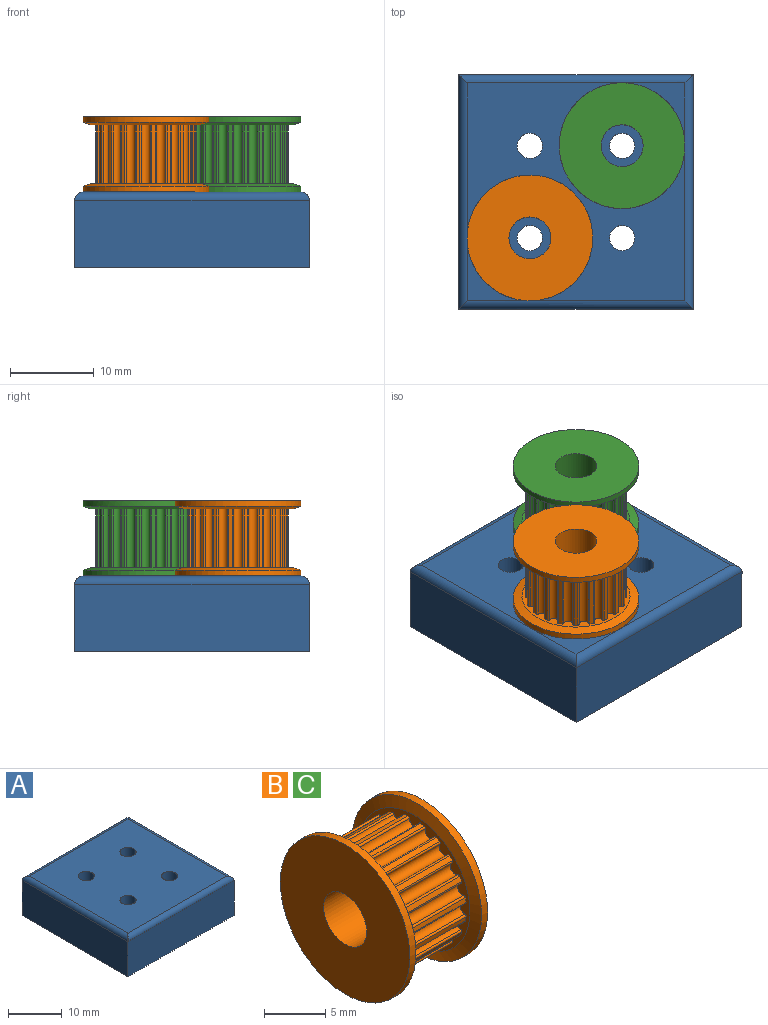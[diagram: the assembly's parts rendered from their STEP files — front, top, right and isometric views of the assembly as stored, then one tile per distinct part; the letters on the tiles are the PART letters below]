
ASSEMBLY  parts=3 mates=2
PART A: 14 faces, bbox 28x28x9 mm
  f0: plane 28x8mm, normal (0,-1,0), area 224mm2, adj f1,f3,f5,f10
  f1: plane 28x8mm, normal (1,0,0), area 224mm2, adj f0,f2,f5,f11
  f2: plane 28x8mm, normal (0,1,0), area 224mm2, adj f1,f3,f5,f13
  f3: plane 28x8mm, normal (-1,0,0), area 224mm2, adj f0,f2,f5,f12
  f4: plane 26x26mm, normal (0,0,1), area 647.7mm2, adj f6,f7,f8,f9,f10,f11,f12,f13
  f5: plane 28x28mm, normal (0,0,-1), area 755.7mm2, adj f0,f1,f2,f3,f6,f7,f8,f9
  f6: cylinder r=1.5mm len=9mm, axis (0,0,1), area 84.8mm2, adj f4,f5
  f7: cylinder r=1.5mm len=9mm, axis (0,0,1), area 84.8mm2, adj f4,f5
  f8: cylinder r=1.5mm len=9mm, axis (0,0,1), area 84.8mm2, adj f4,f5
  f9: cylinder r=1.5mm len=9mm, axis (0,0,1), area 84.8mm2, adj f4,f5
  f10: cylinder r=1mm len=28mm, axis (-1,0,0), area 42.8mm2, adj f0,f4,f11,f12
  f11: cylinder r=1mm len=28mm, axis (0,-1,0), area 42.8mm2, adj f1,f4,f10,f13
  f12: cylinder r=1mm len=28mm, axis (0,1,0), area 42.8mm2, adj f3,f4,f10,f13
  f13: cylinder r=1mm len=28mm, axis (1,0,0), area 42.8mm2, adj f2,f4,f11,f12
PART B: 93 faces, bbox 9x15x15 mm
  f0: cylinder r=7.5mm len=15mm, axis (-1,0,0), area 33.3mm2, adj f25,f92
  f1: cylinder r=2.5mm len=8.8mm, axis (1,0,0), area 138.2mm2, adj f91,f92
  f2: cylinder r=6.05mm len=7mm, axis (-1,0,0), area 3.2mm2, adj f23,f24,f83,f90
  f3: cylinder r=6.05mm len=7mm, axis (-1,0,0), area 3.2mm2, adj f23,f24,f82,f84
  f4: cylinder r=6.05mm len=7mm, axis (-1,0,0), area 3.2mm2, adj f23,f24,f81,f85
  f5: cylinder r=6.05mm len=7mm, axis (-1,0,0), area 3.2mm2, adj f23,f24,f80,f88
  f6: cylinder r=6.05mm len=7mm, axis (-1,0,0), area 3.2mm2, adj f23,f24,f79,f87
  f7: cylinder r=6.05mm len=7mm, axis (-1,0,0), area 3.2mm2, adj f23,f24,f78,f86
  f8: cylinder r=6.05mm len=7mm, axis (-1,0,0), area 3.2mm2, adj f23,f24,f76,f77
  f9: cylinder r=6.05mm len=7mm, axis (-1,0,0), area 3.2mm2, adj f23,f24,f74,f75
  f10: cylinder r=6.05mm len=7mm, axis (-1,0,0), area 3.2mm2, adj f23,f24,f72,f73
  f11: cylinder r=6.05mm len=7mm, axis (-1,0,0), area 3.2mm2, adj f23,f24,f70,f71
  f12: cylinder r=6.05mm len=7mm, axis (-1,0,0), area 3.2mm2, adj f23,f24,f68,f69
  f13: cylinder r=6.05mm len=7mm, axis (-1,0,0), area 3.2mm2, adj f23,f24,f66,f67
  f14: cylinder r=6.05mm len=7mm, axis (-1,0,0), area 3.2mm2, adj f23,f24,f64,f65
  f15: cylinder r=6.05mm len=7mm, axis (-1,0,0), area 3.2mm2, adj f23,f24,f62,f63
  f16: cylinder r=6.05mm len=7mm, axis (-1,0,0), area 3.2mm2, adj f23,f24,f60,f61
  f17: cylinder r=6.05mm len=7mm, axis (-1,0,0), area 3.2mm2, adj f23,f24,f51,f89
  f18: cylinder r=6.05mm len=7mm, axis (-1,0,0), area 3.2mm2, adj f23,f24,f58,f59
  f19: cylinder r=6.05mm len=7mm, axis (-1,0,0), area 3.2mm2, adj f23,f24,f56,f57
  f20: cylinder r=6.05mm len=7mm, axis (-1,0,0), area 3.2mm2, adj f23,f24,f54,f55
  f21: cylinder r=6.05mm len=7mm, axis (-1,0,0), area 3.2mm2, adj f23,f24,f52,f53
  f22: cone r=6.45mm half-angle=74.4deg, axis (1,0,0), area 47.8mm2, adj f23,f30
  f23: plane 12.9x12.9mm, normal (-1,0,0), area 29.5mm2, adj f2,f3,f4,f5,f6,f7,f8,f9
  f24: plane 12.9x12.9mm, normal (1,0,0), area 29.5mm2, adj f2,f3,f4,f5,f6,f7,f8,f9
  f25: cone r=7.5mm half-angle=74.4deg, axis (-1,0,0), area 47.8mm2, adj f0,f24
  f26: plane 8.34x8.34mm, normal (1,0,0), area 31.7mm2, adj f27,f91
  f27: cone r=4.25mm half-angle=45.3deg, axis (-1,0,0), area 3mm2, adj f26,f28
  f28: cone r=4.33mm half-angle=44.7deg, axis (1,0,0), area 3mm2, adj f27,f29
  f29: plane 15x15mm, normal (1,0,0), area 117.9mm2, adj f28,f30
  f30: cylinder r=7.5mm len=15mm, axis (-1,0,0), area 33.3mm2, adj f22,f29
  f31: cylinder r=0.55mm len=7mm, axis (-1,0,0), area 12.1mm2, adj f23,f24,f51,f52
  f32: cylinder r=0.55mm len=7mm, axis (-1,0,0), area 12.1mm2, adj f23,f24,f53,f54
  f33: cylinder r=0.55mm len=7mm, axis (-1,0,0), area 12.1mm2, adj f23,f24,f55,f56
  f34: cylinder r=0.55mm len=7mm, axis (-1,0,0), area 12.1mm2, adj f23,f24,f57,f58
  f35: cylinder r=0.55mm len=7mm, axis (-1,0,0), area 12.1mm2, adj f23,f24,f59,f60
  f36: cylinder r=0.55mm len=7mm, axis (-1,0,0), area 12.1mm2, adj f23,f24,f89,f90
  f37: cylinder r=0.55mm len=7mm, axis (-1,0,0), area 12.1mm2, adj f23,f24,f61,f62
  f38: cylinder r=0.55mm len=7mm, axis (-1,0,0), area 12.1mm2, adj f23,f24,f63,f64
  f39: cylinder r=0.55mm len=7mm, axis (-1,0,0), area 12.1mm2, adj f23,f24,f65,f66
  f40: cylinder r=0.55mm len=7mm, axis (-1,0,0), area 12.1mm2, adj f23,f24,f67,f68
  f41: cylinder r=0.55mm len=7mm, axis (-1,0,0), area 12.1mm2, adj f23,f24,f69,f70
  f42: cylinder r=0.55mm len=7mm, axis (-1,0,0), area 12.1mm2, adj f23,f24,f71,f72
  f43: cylinder r=0.55mm len=7mm, axis (-1,0,0), area 12.1mm2, adj f23,f24,f73,f74
  f44: cylinder r=0.55mm len=7mm, axis (-1,0,0), area 12.1mm2, adj f23,f24,f75,f76
  f45: cylinder r=0.55mm len=7mm, axis (-1,0,0), area 12.1mm2, adj f23,f24,f77,f78
  f46: cylinder r=0.55mm len=7mm, axis (-1,0,0), area 12.1mm2, adj f23,f24,f79,f86
  f47: cylinder r=0.55mm len=7mm, axis (-1,0,0), area 12.1mm2, adj f23,f24,f80,f87
  f48: cylinder r=0.55mm len=7mm, axis (-1,0,0), area 12.1mm2, adj f23,f24,f81,f88
  f49: cylinder r=0.55mm len=7mm, axis (-1,0,0), area 12.1mm2, adj f23,f24,f82,f85
  f50: cylinder r=0.55mm len=7mm, axis (-1,0,0), area 12.1mm2, adj f23,f24,f83,f84
  f51: cylinder r=0.15mm len=7mm, axis (1,0,0), area 1.8mm2, adj f17,f23,f24,f31
  f52: cylinder r=0.15mm len=7mm, axis (-1,0,0), area 1.8mm2, adj f21,f23,f24,f31
  f53: cylinder r=0.15mm len=7mm, axis (1,0,0), area 1.8mm2, adj f21,f23,f24,f32
  f54: cylinder r=0.15mm len=7mm, axis (-1,0,0), area 1.8mm2, adj f20,f23,f24,f32
  f55: cylinder r=0.15mm len=7mm, axis (1,0,0), area 1.8mm2, adj f20,f23,f24,f33
  f56: cylinder r=0.15mm len=7mm, axis (-1,0,0), area 1.8mm2, adj f19,f23,f24,f33
  f57: cylinder r=0.15mm len=7mm, axis (1,0,0), area 1.8mm2, adj f19,f23,f24,f34
  f58: cylinder r=0.15mm len=7mm, axis (-1,0,0), area 1.8mm2, adj f18,f23,f24,f34
  f59: cylinder r=0.15mm len=7mm, axis (1,0,0), area 1.8mm2, adj f18,f23,f24,f35
  f60: cylinder r=0.15mm len=7mm, axis (-1,0,0), area 1.8mm2, adj f16,f23,f24,f35
  f61: cylinder r=0.15mm len=7mm, axis (1,0,0), area 1.8mm2, adj f16,f23,f24,f37
  f62: cylinder r=0.15mm len=7mm, axis (-1,0,0), area 1.8mm2, adj f15,f23,f24,f37
  f63: cylinder r=0.15mm len=7mm, axis (1,0,0), area 1.8mm2, adj f15,f23,f24,f38
  f64: cylinder r=0.15mm len=7mm, axis (-1,0,0), area 1.8mm2, adj f14,f23,f24,f38
  f65: cylinder r=0.15mm len=7mm, axis (1,0,0), area 1.8mm2, adj f14,f23,f24,f39
  f66: cylinder r=0.15mm len=7mm, axis (-1,0,0), area 1.8mm2, adj f13,f23,f24,f39
  f67: cylinder r=0.15mm len=7mm, axis (1,0,0), area 1.8mm2, adj f13,f23,f24,f40
  f68: cylinder r=0.15mm len=7mm, axis (-1,0,0), area 1.8mm2, adj f12,f23,f24,f40
  f69: cylinder r=0.15mm len=7mm, axis (1,0,0), area 1.8mm2, adj f12,f23,f24,f41
  f70: cylinder r=0.15mm len=7mm, axis (-1,0,0), area 1.8mm2, adj f11,f23,f24,f41
  f71: cylinder r=0.15mm len=7mm, axis (1,0,0), area 1.8mm2, adj f11,f23,f24,f42
  f72: cylinder r=0.15mm len=7mm, axis (-1,0,0), area 1.8mm2, adj f10,f23,f24,f42
  f73: cylinder r=0.15mm len=7mm, axis (1,0,0), area 1.8mm2, adj f10,f23,f24,f43
  f74: cylinder r=0.15mm len=7mm, axis (-1,0,0), area 1.8mm2, adj f9,f23,f24,f43
  f75: cylinder r=0.15mm len=7mm, axis (1,0,0), area 1.8mm2, adj f9,f23,f24,f44
  f76: cylinder r=0.15mm len=7mm, axis (-1,0,0), area 1.8mm2, adj f8,f23,f24,f44
  f77: cylinder r=0.15mm len=7mm, axis (1,0,0), area 1.8mm2, adj f8,f23,f24,f45
  f78: cylinder r=0.15mm len=7mm, axis (-1,0,0), area 1.8mm2, adj f7,f23,f24,f45
  f79: cylinder r=0.15mm len=7mm, axis (-1,0,0), area 1.8mm2, adj f6,f23,f24,f46
  f80: cylinder r=0.15mm len=7mm, axis (-1,0,0), area 1.8mm2, adj f5,f23,f24,f47
  f81: cylinder r=0.15mm len=7mm, axis (-1,0,0), area 1.8mm2, adj f4,f23,f24,f48
  f82: cylinder r=0.15mm len=7mm, axis (-1,0,0), area 1.8mm2, adj f3,f23,f24,f49
  f83: cylinder r=0.15mm len=7mm, axis (-1,0,0), area 1.8mm2, adj f2,f23,f24,f50
  f84: cylinder r=0.15mm len=7mm, axis (1,0,0), area 1.8mm2, adj f3,f23,f24,f50
  f85: cylinder r=0.15mm len=7mm, axis (1,0,0), area 1.8mm2, adj f4,f23,f24,f49
  f86: cylinder r=0.15mm len=7mm, axis (1,0,0), area 1.8mm2, adj f7,f23,f24,f46
  f87: cylinder r=0.15mm len=7mm, axis (1,0,0), area 1.8mm2, adj f6,f23,f24,f47
  f88: cylinder r=0.15mm len=7mm, axis (1,0,0), area 1.8mm2, adj f5,f23,f24,f48
  f89: cylinder r=0.15mm len=7mm, axis (-1,0,0), area 1.8mm2, adj f17,f23,f24,f36
  f90: cylinder r=0.15mm len=7mm, axis (1,0,0), area 1.8mm2, adj f2,f23,f24,f36
  f91: cone r=2.5mm half-angle=45deg, axis (1,0,0), area 4.6mm2, adj f1,f26
  f92: plane 15x15mm, normal (-1,0,0), area 157.1mm2, adj f0,f1
PART C: same geometry as B
PLACE A rot(axis=(-0.03,0.75,0.66),0deg) t=(-138.5,-139,3)mm
PLACE B rot(axis=(0.58,0.58,-0.58),120deg) t=(-144,-144.5,26)mm
PLACE C rot(axis=(0,1,0),90deg) t=(-133,-133.5,26)mm
MATE fastened C.f0 <-> A.f6  axis (0,0,-1) through (-133,-133.5,12)mm
MATE fastened B.f0 <-> A.f8  axis (0,0,-1) through (-144,-144.5,12)mm
